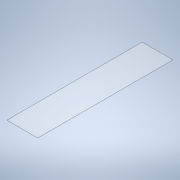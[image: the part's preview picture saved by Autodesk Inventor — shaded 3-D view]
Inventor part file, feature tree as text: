
AUTODESK INVENTOR PART (.ipt)
format: ipt  version: 2020 (Build 240168000, 168)  size: 94,208 bytes
history: native  units: in
note: dims shown in document units (in); Inventor stores cm internally (conversion verified against a paired STEP export)
features: extrude x1, sketch x1
ambient origin geometry x8: Origin, YZ Plane, XZ Plane, XY Plane, X Axis, Y Axis, Z Axis, Center Point
bodies: Solid1 (feature_tree)
feature tree (2):
  extrude  "Extrusion1"  Depth=17.5in
  sketch  "Sketch1"  dims[d0=4.0in d1=17.5in d2=0.04in d3=0.0in]
